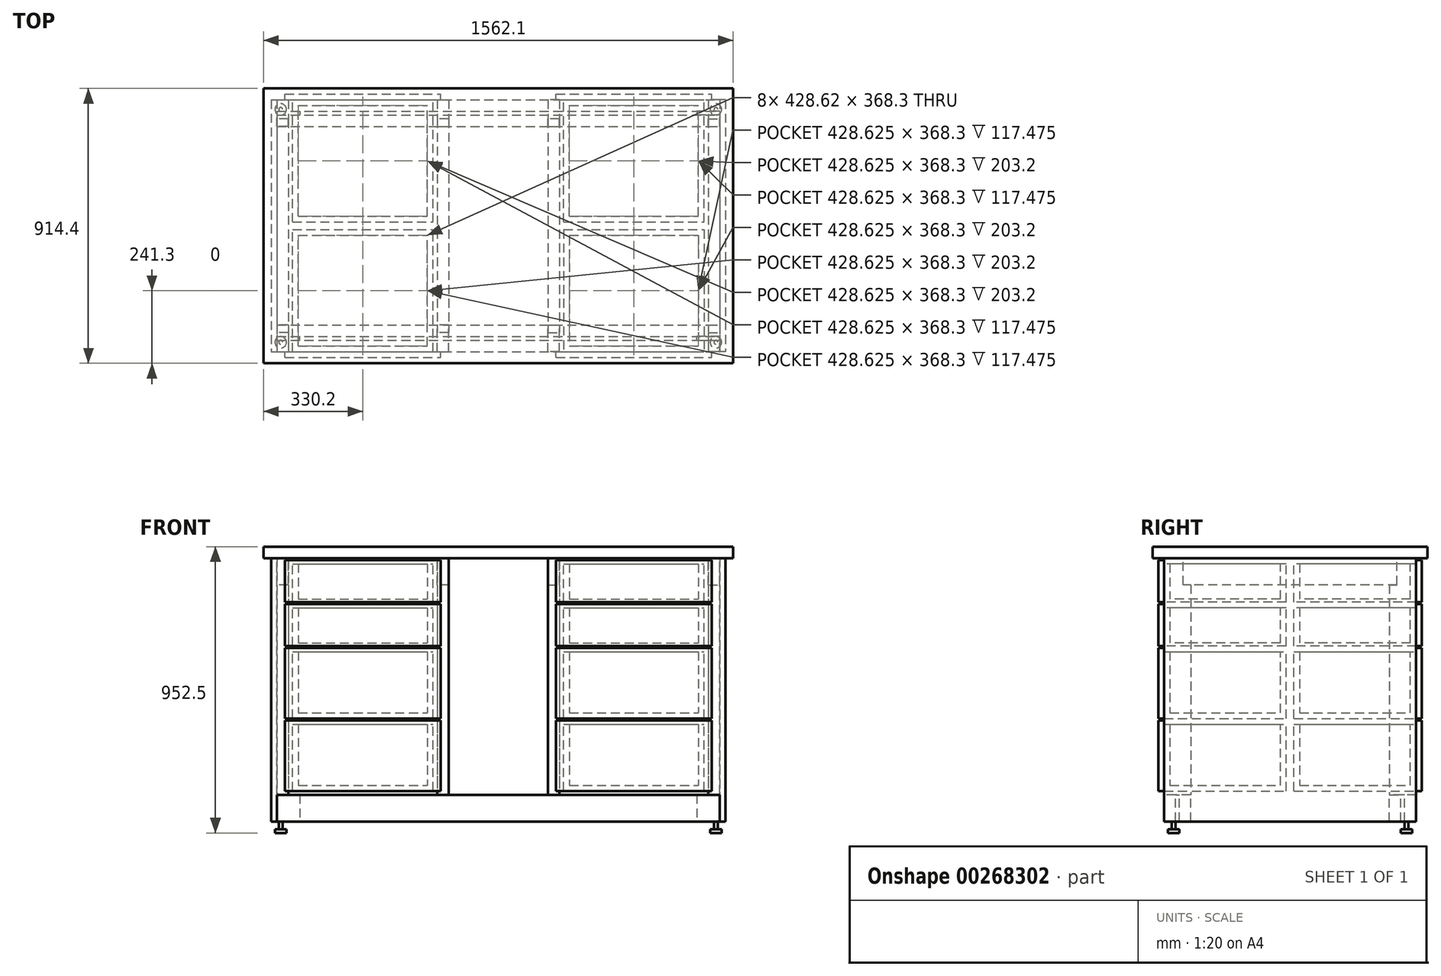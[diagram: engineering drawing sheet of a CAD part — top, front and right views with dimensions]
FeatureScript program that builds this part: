
annotation { "Feature Type Name" : "Feature", "Feature Type Description" : "" }
export const myFeature = defineFeature(function(context is Context, id is Id, definition is map)
    precondition{}
    {
        {
            var Q0;
            Q0=qCreatedBy(makeId("Top.planeOp"),FACE);
            var sketch = newSketch(context, id + "F0", { "sketchPlane" : qUnion([Q0])});
            skLineSegment(sketch, "E0.bottom", {"start": v(-736.6, 419.1) * mm, "end": v(-698.5, 419.1) * mm});
            skLineSegment(sketch, "E0.top", {"start": v(-736.6, 330.2) * mm, "end": v(-698.5, 330.2) * mm});
            skLineSegment(sketch, "E0.left", {"start": v(-736.6, 419.1) * mm, "end": v(-736.6, 330.2) * mm});
            skLineSegment(sketch, "E0.right", {"start": v(-698.5, 419.1) * mm, "end": v(-698.5, 330.2) * mm});
            skLineSegment(sketch, "E1.bottom", {"start": v(-736.6, -330.2) * mm, "end": v(-698.5, -330.2) * mm});
            skLineSegment(sketch, "E1.top", {"start": v(-736.6, -419.1) * mm, "end": v(-698.5, -419.1) * mm});
            skLineSegment(sketch, "E1.left", {"start": v(-736.6, -330.2) * mm, "end": v(-736.6, -419.1) * mm});
            skLineSegment(sketch, "E1.right", {"start": v(-698.5, -330.2) * mm, "end": v(-698.5, -419.1) * mm});
            skLineSegment(sketch, "E2.MirrorCS", {"start": v(698.5, 419.1) * mm, "end": v(698.5, 330.2) * mm});
            skLineSegment(sketch, "E3.MirrorCS", {"start": v(736.6, 330.2) * mm, "end": v(698.5, 330.2) * mm});
            skLineSegment(sketch, "E4.MirrorCS", {"start": v(736.6, 419.1) * mm, "end": v(736.6, 330.2) * mm});
            skLineSegment(sketch, "E5.MirrorCS", {"start": v(736.6, 419.1) * mm, "end": v(698.5, 419.1) * mm});
            skLineSegment(sketch, "E6.MirrorCS", {"start": v(736.6, -330.2) * mm, "end": v(698.5, -330.2) * mm});
            skLineSegment(sketch, "E7.MirrorCS", {"start": v(698.5, -330.2) * mm, "end": v(698.5, -419.1) * mm});
            skLineSegment(sketch, "E8.MirrorCS", {"start": v(736.6, -330.2) * mm, "end": v(736.6, -419.1) * mm});
            skLineSegment(sketch, "E9.MirrorCS", {"start": v(736.6, -419.1) * mm, "end": v(698.5, -419.1) * mm});
            skLineSegment(sketch, "E10.bottom", {"start": v(-203.2, 419.1) * mm, "end": v(-165.1, 419.1) * mm});
            skLineSegment(sketch, "E10.top", {"start": v(-203.2, 330.2) * mm, "end": v(-165.1, 330.2) * mm});
            skLineSegment(sketch, "E10.left", {"start": v(-203.2, 419.1) * mm, "end": v(-203.2, 330.2) * mm});
            skLineSegment(sketch, "E10.right", {"start": v(-165.1, 419.1) * mm, "end": v(-165.1, 330.2) * mm});
            skLineSegment(sketch, "E11.MirrorCS", {"start": v(-165.1, -419.1) * mm, "end": v(-165.1, -330.2) * mm});
            skLineSegment(sketch, "E12.MirrorCS", {"start": v(-203.2, -330.2) * mm, "end": v(-165.1, -330.2) * mm});
            skLineSegment(sketch, "E13.MirrorCS", {"start": v(-203.2, -419.1) * mm, "end": v(-203.2, -330.2) * mm});
            skLineSegment(sketch, "E14.MirrorCS", {"start": v(-203.2, -419.1) * mm, "end": v(-165.1, -419.1) * mm});
            skLineSegment(sketch, "E15", {"start": v(-736.6, 419.1) * mm, "end": v(736.6, 419.1) * mm, "construction": true});
            skLineSegment(sketch, "E16.MirrorCS", {"start": v(203.2, 330.2) * mm, "end": v(165.1, 330.2) * mm});
            skLineSegment(sketch, "E17.MirrorCS", {"start": v(203.2, 419.1) * mm, "end": v(165.1, 419.1) * mm});
            skLineSegment(sketch, "E18.MirrorCS", {"start": v(165.1, 419.1) * mm, "end": v(165.1, 330.2) * mm});
            skLineSegment(sketch, "E19.MirrorCS", {"start": v(203.2, 419.1) * mm, "end": v(203.2, 330.2) * mm});
            skLineSegment(sketch, "E20.MirrorCS", {"start": v(203.2, -419.1) * mm, "end": v(165.1, -419.1) * mm});
            skLineSegment(sketch, "E21.MirrorCS", {"start": v(165.1, -419.1) * mm, "end": v(165.1, -330.2) * mm});
            skLineSegment(sketch, "E22.MirrorCS", {"start": v(203.2, -330.2) * mm, "end": v(165.1, -330.2) * mm});
            skLineSegment(sketch, "E23.MirrorCS", {"start": v(203.2, -419.1) * mm, "end": v(203.2, -330.2) * mm});
            skSolve(sketch);
        }
        {
            var Q0;
            Q0=makeQuery(id+"F0.imprint","IMPRINT",FACE,{"disambiguationData":[TD([[makeQuery(id+"F0.imprint","IMPRINT",EDGE,{"derivedFrom":sQuery(id+"F0.wireOp",EDGE,"E0.bottom")}),-1.0]])]});
            var Q1;
            Q1=makeQuery(id+"F0.imprint","IMPRINT",FACE,{"disambiguationData":[TD([[makeQuery(id+"F0.imprint","IMPRINT",EDGE,{"derivedFrom":sQuery(id+"F0.wireOp",EDGE,"E2.MirrorCS")}),1.0]])]});
            var Q2;
            Q2=makeQuery(id+"F0.imprint","IMPRINT",FACE,{"disambiguationData":[TD([[makeQuery(id+"F0.imprint","IMPRINT",EDGE,{"derivedFrom":sQuery(id+"F0.wireOp",EDGE,"E6.MirrorCS")}),1.0]])]});
            var Q3;
            Q3=makeQuery(id+"F0.imprint","IMPRINT",FACE,{"disambiguationData":[TD([[makeQuery(id+"F0.imprint","IMPRINT",EDGE,{"derivedFrom":sQuery(id+"F0.wireOp",EDGE,"E1.bottom")}),-1.0]])]});
            var Q4;
            Q4=makeQuery(id+"F0.imprint","IMPRINT",FACE,{"disambiguationData":[TD([[makeQuery(id+"F0.imprint","IMPRINT",EDGE,{"derivedFrom":sQuery(id+"F0.wireOp",EDGE,"E10.bottom")}),-1.0]])]});
            var Q5;
            Q5=makeQuery(id+"F0.imprint","IMPRINT",FACE,{"disambiguationData":[TD([[makeQuery(id+"F0.imprint","IMPRINT",EDGE,{"derivedFrom":sQuery(id+"F0.wireOp",EDGE,"E16.MirrorCS")}),-1.0]])]});
            var Q6;
            Q6=makeQuery(id+"F0.imprint","IMPRINT",FACE,{"disambiguationData":[TD([[makeQuery(id+"F0.imprint","IMPRINT",EDGE,{"derivedFrom":sQuery(id+"F0.wireOp",EDGE,"E20.MirrorCS")}),-1.0]])]});
            var Q7;
            Q7=makeQuery(id+"F0.imprint","IMPRINT",FACE,{"disambiguationData":[TD([[makeQuery(id+"F0.imprint","IMPRINT",EDGE,{"derivedFrom":sQuery(id+"F0.wireOp",EDGE,"E11.MirrorCS")}),1.0]])]});
            extrude(context, id + "F1", {"entities" : qUnion([Q0, Q1, Q2, Q3, Q4, Q5, Q6, Q7]), "depth" : 787.4 * mm});
        }
        {
            var Q0;
            Q0=makeQuery(id+"F1.opExtrude","CAP_FACE",FACE,{"disambiguationData":[OSD([sQuery(id+"F0.wireOp",EDGE,"E1.bottom"),sQuery(id+"F0.wireOp",EDGE,"E1.top"),sQuery(id+"F0.wireOp",EDGE,"E1.left"),sQuery(id+"F0.wireOp",EDGE,"E1.right")])],"isStart":true});
            var sketch = newSketch(context, id + "F2", { "sketchPlane" : qUnion([Q0])});
            skLineSegment(sketch, "E24.bottom", {"start": v(-736.6, 419.1) * mm, "end": v(736.6, 419.1) * mm});
            skLineSegment(sketch, "E24.top", {"start": v(-736.6, 381) * mm, "end": v(736.6, 381) * mm});
            skLineSegment(sketch, "E24.left", {"start": v(-736.6, 419.1) * mm, "end": v(-736.6, 381) * mm});
            skLineSegment(sketch, "E24.right", {"start": v(736.6, 419.1) * mm, "end": v(736.6, 381) * mm});
            skLineSegment(sketch, "E25.bottom", {"start": v(-736.6, 330.2) * mm, "end": v(736.6, 330.2) * mm});
            skLineSegment(sketch, "E25.top", {"start": v(-736.6, 368.3) * mm, "end": v(736.6, 368.3) * mm});
            skLineSegment(sketch, "E25.left", {"start": v(-736.6, 330.2) * mm, "end": v(-736.6, 368.3) * mm});
            skLineSegment(sketch, "E25.right", {"start": v(736.6, 330.2) * mm, "end": v(736.6, 368.3) * mm});
            skLineSegment(sketch, "E26.MirrorCS", {"start": v(-736.6, -330.2) * mm, "end": v(736.6, -330.2) * mm});
            skLineSegment(sketch, "E27.MirrorCS", {"start": v(-736.6, -368.3) * mm, "end": v(736.6, -368.3) * mm});
            skLineSegment(sketch, "E28.MirrorCS", {"start": v(-736.6, -330.2) * mm, "end": v(-736.6, -368.3) * mm});
            skLineSegment(sketch, "E29.MirrorCS", {"start": v(736.6, -330.2) * mm, "end": v(736.6, -368.3) * mm});
            skLineSegment(sketch, "E30.MirrorCS", {"start": v(736.6, -419.1) * mm, "end": v(736.6, -381) * mm});
            skLineSegment(sketch, "E31.MirrorCS", {"start": v(-736.6, -419.1) * mm, "end": v(736.6, -419.1) * mm});
            skLineSegment(sketch, "E32.MirrorCS", {"start": v(-736.6, -381) * mm, "end": v(736.6, -381) * mm});
            skLineSegment(sketch, "E33.MirrorCS", {"start": v(-736.6, -419.1) * mm, "end": v(-736.6, -381) * mm});
            skSolve(sketch);
        }
        {
            var Q0;
            {var subQ0=sQuery(id+"F2.wireOp",EDGE,"E25.left");Q0=makeQuery(id+"F2.imprint","IMPRINT",FACE,{"disambiguationData":[TD([[makeQuery(id+"F2.imprint","IMPRINT",EDGE,{"derivedFrom":subQ0}),-1.0]])]});}
            var Q1;
            {var subQ3=sQuery(id+"F2.wireOp",EDGE,"E25.right");Q1=makeQuery(id+"F2.imprint","IMPRINT",FACE,{"disambiguationData":[TD([[makeQuery(id+"F2.imprint","IMPRINT",EDGE,{"derivedFrom":subQ3}),1.0]])]});}
            var Q2;
            {var subQ3=sQuery(id+"F2.wireOp",EDGE,"E24.right");Q2=makeQuery(id+"F2.imprint","IMPRINT",FACE,{"disambiguationData":[TD([[makeQuery(id+"F2.imprint","IMPRINT",EDGE,{"derivedFrom":subQ3}),-1.0]])]});}
            var Q3;
            {var subQ0=sQuery(id+"F2.wireOp",EDGE,"E24.left");Q3=makeQuery(id+"F2.imprint","IMPRINT",FACE,{"disambiguationData":[TD([[makeQuery(id+"F2.imprint","IMPRINT",EDGE,{"derivedFrom":subQ0}),-1.0]])]});}
            var Q4;
            Q4=makeQuery(id+"F2.imprint","IMPRINT",FACE,{"disambiguationData":[TD([[makeQuery(id+"F2.imprint","IMPRINT",EDGE,{"derivedFrom":sQuery(id+"F2.wireOp",EDGE,"E26.MirrorCS")}),-1.0]])]});
            var Q5;
            Q5=makeQuery(id+"F2.imprint","IMPRINT",FACE,{"disambiguationData":[TD([[makeQuery(id+"F2.imprint","IMPRINT",EDGE,{"derivedFrom":sQuery(id+"F2.wireOp",EDGE,"E30.MirrorCS")}),1.0]])]});
            extrude(context, id + "F3", {"entities" : qUnion([Q0, Q1, Q2, Q3, Q4, Q5]), "depth" : 88.9 * mm});
        }
        {
            var Q0;
            Q0=makeQuery(id+"F1.opExtrude","CAP_FACE",FACE,{"disambiguationData":[OSD([sQuery(id+"F0.wireOp",EDGE,"E0.bottom"),sQuery(id+"F0.wireOp",EDGE,"E0.top"),sQuery(id+"F0.wireOp",EDGE,"E0.left"),sQuery(id+"F0.wireOp",EDGE,"E0.right")])],"isStart":false});
            var sketch = newSketch(context, id + "F4", { "sketchPlane" : qUnion([Q0])});
            skLineSegment(sketch, "E34.bottom", {"start": v(-755.65, 419.1) * mm, "end": v(-736.6, 419.1) * mm});
            skLineSegment(sketch, "E34.top", {"start": v(-755.65, -419.1) * mm, "end": v(-736.6, -419.1) * mm});
            skLineSegment(sketch, "E34.left", {"start": v(-755.65, 419.1) * mm, "end": v(-755.65, -419.1) * mm});
            skLineSegment(sketch, "E34.right", {"start": v(-736.6, 419.1) * mm, "end": v(-736.6, -419.1) * mm});
            skLineSegment(sketch, "E35.MirrorCS", {"start": v(755.65, 419.1) * mm, "end": v(736.6, 419.1) * mm});
            skLineSegment(sketch, "E36.MirrorCS", {"start": v(755.65, -419.1) * mm, "end": v(736.6, -419.1) * mm});
            skLineSegment(sketch, "E37.MirrorCS", {"start": v(736.6, 419.1) * mm, "end": v(736.6, -419.1) * mm});
            skLineSegment(sketch, "E38.MirrorCS", {"start": v(755.65, 419.1) * mm, "end": v(755.65, -419.1) * mm});
            skSolve(sketch);
        }
        {
            var Q0;
            Q0=makeQuery(id+"F4.imprint","IMPRINT",FACE,{"disambiguationData":[TD([[makeQuery(id+"F4.imprint","IMPRINT",EDGE,{"derivedFrom":sQuery(id+"F4.wireOp",EDGE,"E35.MirrorCS")}),1.0]])]});
            var Q1;
            {var subQ3=sQuery(id+"F4.wireOp",EDGE,"E34.bottom");Q1=makeQuery(id+"F4.imprint","IMPRINT",FACE,{"disambiguationData":[TD([[makeQuery(id+"F4.imprint","IMPRINT",EDGE,{"derivedFrom":subQ3}),-1.0]])]});}
            var Q2;
            Q2=makeQuery(id+"F3.opExtrude","CAP_FACE",FACE,{"disambiguationData":[OSD([sQuery(id+"F2.wireOp",EDGE,"E30.MirrorCS"),sQuery(id+"F2.wireOp",EDGE,"E31.MirrorCS"),sQuery(id+"F2.wireOp",EDGE,"E32.MirrorCS"),sQuery(id+"F2.wireOp",EDGE,"E33.MirrorCS")])],"isStart":false});
            extrude(context, id + "F5", {"entities" : qUnion([Q0, Q1]), "oppositeDirection" : true, "endBoundEntityFace" : qUnion([Q2]), "depth" : 876.3 * mm});
        }
        {
            var Q0;
            Q0=makeQuery(id+"F1.opExtrude","CAP_FACE",FACE,{"disambiguationData":[OSD([sQuery(id+"F0.wireOp",EDGE,"E10.bottom"),sQuery(id+"F0.wireOp",EDGE,"E10.top"),sQuery(id+"F0.wireOp",EDGE,"E10.left"),sQuery(id+"F0.wireOp",EDGE,"E10.right")])],"isStart":false});
            var sketch = newSketch(context, id + "F6", { "sketchPlane" : qUnion([Q0])});
            skLineSegment(sketch, "E39.bottom", {"start": v(-698.5, 330.2) * mm, "end": v(-736.6, 330.2) * mm});
            skLineSegment(sketch, "E39.top", {"start": v(-698.5, 355.6) * mm, "end": v(-736.6, 355.6) * mm});
            skLineSegment(sketch, "E39.left", {"start": v(-698.5, 330.2) * mm, "end": v(-698.5, 355.6) * mm});
            skLineSegment(sketch, "E39.right", {"start": v(-736.6, 330.2) * mm, "end": v(-736.6, 355.6) * mm});
            skLineSegment(sketch, "E40.bottom", {"start": v(-165.1, 330.2) * mm, "end": v(-203.2, 330.2) * mm});
            skLineSegment(sketch, "E40.top", {"start": v(-165.1, 355.6) * mm, "end": v(-203.2, 355.6) * mm});
            skLineSegment(sketch, "E40.left", {"start": v(-165.1, 330.2) * mm, "end": v(-165.1, 355.6) * mm});
            skLineSegment(sketch, "E40.right", {"start": v(-203.2, 330.2) * mm, "end": v(-203.2, 355.6) * mm});
            skLineSegment(sketch, "E41.MirrorCS", {"start": v(203.2, 330.2) * mm, "end": v(203.2, 355.6) * mm});
            skLineSegment(sketch, "E42.MirrorCS", {"start": v(165.1, 330.2) * mm, "end": v(165.1, 355.6) * mm});
            skLineSegment(sketch, "E43.MirrorCS", {"start": v(698.5, 330.2) * mm, "end": v(698.5, 355.6) * mm});
            skLineSegment(sketch, "E44.MirrorCS", {"start": v(736.6, 330.2) * mm, "end": v(736.6, 355.6) * mm});
            skLineSegment(sketch, "E45.MirrorCS", {"start": v(698.5, 355.6) * mm, "end": v(736.6, 355.6) * mm});
            skLineSegment(sketch, "E46.MirrorCS", {"start": v(165.1, 330.2) * mm, "end": v(203.2, 330.2) * mm});
            skLineSegment(sketch, "E47.MirrorCS", {"start": v(698.5, 330.2) * mm, "end": v(736.6, 330.2) * mm});
            skLineSegment(sketch, "E48.MirrorCS", {"start": v(165.1, 355.6) * mm, "end": v(203.2, 355.6) * mm});
            skLineSegment(sketch, "E49.MirrorCS", {"start": v(736.6, -330.2) * mm, "end": v(736.6, -355.6) * mm});
            skLineSegment(sketch, "E50.MirrorCS", {"start": v(698.5, -330.2) * mm, "end": v(698.5, -355.6) * mm});
            skLineSegment(sketch, "E51.MirrorCS", {"start": v(165.1, -330.2) * mm, "end": v(165.1, -355.6) * mm});
            skLineSegment(sketch, "E52.MirrorCS", {"start": v(203.2, -330.2) * mm, "end": v(203.2, -355.6) * mm});
            skLineSegment(sketch, "E53.MirrorCS", {"start": v(-203.2, -330.2) * mm, "end": v(-203.2, -355.6) * mm});
            skLineSegment(sketch, "E54.MirrorCS", {"start": v(-165.1, -330.2) * mm, "end": v(-165.1, -355.6) * mm});
            skLineSegment(sketch, "E55.MirrorCS", {"start": v(-698.5, -330.2) * mm, "end": v(-698.5, -355.6) * mm});
            skLineSegment(sketch, "E56.MirrorCS", {"start": v(-736.6, -330.2) * mm, "end": v(-736.6, -355.6) * mm});
            skLineSegment(sketch, "E57.MirrorCS", {"start": v(698.5, -355.6) * mm, "end": v(736.6, -355.6) * mm});
            skLineSegment(sketch, "E58.MirrorCS", {"start": v(-165.1, -355.6) * mm, "end": v(-203.2, -355.6) * mm});
            skLineSegment(sketch, "E59.MirrorCS", {"start": v(165.1, -330.2) * mm, "end": v(203.2, -330.2) * mm});
            skLineSegment(sketch, "E60.MirrorCS", {"start": v(-698.5, -355.6) * mm, "end": v(-736.6, -355.6) * mm});
            skLineSegment(sketch, "E61.MirrorCS", {"start": v(-698.5, -330.2) * mm, "end": v(-736.6, -330.2) * mm});
            skLineSegment(sketch, "E62.MirrorCS", {"start": v(698.5, -330.2) * mm, "end": v(736.6, -330.2) * mm});
            skLineSegment(sketch, "E63.MirrorCS", {"start": v(-165.1, -330.2) * mm, "end": v(-203.2, -330.2) * mm});
            skLineSegment(sketch, "E64.MirrorCS", {"start": v(165.1, -355.6) * mm, "end": v(203.2, -355.6) * mm});
            skSolve(sketch);
        }
        {
            var Q0;
            Q0=makeQuery(id+"F6.imprint","IMPRINT",FACE,{"disambiguationData":[TD([[makeQuery(id+"F6.imprint","IMPRINT",EDGE,{"derivedFrom":sQuery(id+"F6.wireOp",EDGE,"E39.bottom")}),-1.0]])]});
            var Q1;
            Q1=makeQuery(id+"F6.imprint","IMPRINT",FACE,{"disambiguationData":[TD([[makeQuery(id+"F6.imprint","IMPRINT",EDGE,{"derivedFrom":sQuery(id+"F6.wireOp",EDGE,"E40.bottom")}),1.0]])]});
            var Q2;
            Q2=makeQuery(id+"F6.imprint","IMPRINT",FACE,{"disambiguationData":[TD([[makeQuery(id+"F6.imprint","IMPRINT",EDGE,{"derivedFrom":sQuery(id+"F6.wireOp",EDGE,"E41.MirrorCS")}),1.0]])]});
            var Q3;
            Q3=makeQuery(id+"F6.imprint","IMPRINT",FACE,{"disambiguationData":[TD([[makeQuery(id+"F6.imprint","IMPRINT",EDGE,{"derivedFrom":sQuery(id+"F6.wireOp",EDGE,"E43.MirrorCS")}),-1.0]])]});
            var Q4;
            Q4=makeQuery(id+"F6.imprint","IMPRINT",FACE,{"disambiguationData":[TD([[makeQuery(id+"F6.imprint","IMPRINT",EDGE,{"derivedFrom":sQuery(id+"F6.wireOp",EDGE,"E49.MirrorCS")}),-1.0]])]});
            var Q5;
            Q5=makeQuery(id+"F6.imprint","IMPRINT",FACE,{"disambiguationData":[TD([[makeQuery(id+"F6.imprint","IMPRINT",EDGE,{"derivedFrom":sQuery(id+"F6.wireOp",EDGE,"E51.MirrorCS")}),1.0]])]});
            var Q6;
            Q6=makeQuery(id+"F6.imprint","IMPRINT",FACE,{"disambiguationData":[TD([[makeQuery(id+"F6.imprint","IMPRINT",EDGE,{"derivedFrom":sQuery(id+"F6.wireOp",EDGE,"E53.MirrorCS")}),1.0]])]});
            var Q7;
            Q7=makeQuery(id+"F6.imprint","IMPRINT",FACE,{"disambiguationData":[TD([[makeQuery(id+"F6.imprint","IMPRINT",EDGE,{"derivedFrom":sQuery(id+"F6.wireOp",EDGE,"E55.MirrorCS")}),-1.0]])]});
            extrude(context, id + "F7", {"entities" : qUnion([Q0, Q1, Q2, Q3, Q4, Q5, Q6, Q7]), "operationType" : NewBodyOperationType.REMOVE, "oppositeDirection" : true, "depth" : 88.9 * mm});
        }
        {
            var Q0;
            Q0=makeQuery(id+"F7.boolean.opBoolean","COPY",FACE,{"derivedFrom":makeQuery(id+"F7.opExtrude","CAP_FACE",FACE,{"disambiguationData":[OSD([sQuery(id+"F6.wireOp",EDGE,"E39.bottom"),sQuery(id+"F6.wireOp",EDGE,"E39.top"),sQuery(id+"F6.wireOp",EDGE,"E39.left"),sQuery(id+"F6.wireOp",EDGE,"E39.right")])],"isStart":false})});
            var sketch = newSketch(context, id + "F8", { "sketchPlane" : qUnion([Q0])});
            skLineSegment(sketch, "E65.bottom", {"start": v(-736.6, 355.6) * mm, "end": v(-698.5, 355.6) * mm});
            skLineSegment(sketch, "E65.top", {"start": v(-736.6, -355.6) * mm, "end": v(-698.5, -355.6) * mm});
            skLineSegment(sketch, "E65.left", {"start": v(-736.6, 355.6) * mm, "end": v(-736.6, -355.6) * mm});
            skLineSegment(sketch, "E65.right", {"start": v(-698.5, 355.6) * mm, "end": v(-698.5, -355.6) * mm});
            skLineSegment(sketch, "E66.bottom", {"start": v(-203.2, 355.6) * mm, "end": v(-165.1, 355.6) * mm});
            skLineSegment(sketch, "E66.top", {"start": v(-203.2, -355.6) * mm, "end": v(-165.1, -355.6) * mm});
            skLineSegment(sketch, "E66.left", {"start": v(-203.2, 355.6) * mm, "end": v(-203.2, -355.6) * mm});
            skLineSegment(sketch, "E66.right", {"start": v(-165.1, 355.6) * mm, "end": v(-165.1, -355.6) * mm});
            skLineSegment(sketch, "E67.MirrorCS", {"start": v(203.2, 355.6) * mm, "end": v(165.1, 355.6) * mm});
            skLineSegment(sketch, "E68.MirrorCS", {"start": v(203.2, -355.6) * mm, "end": v(165.1, -355.6) * mm});
            skLineSegment(sketch, "E69.MirrorCS", {"start": v(736.6, 355.6) * mm, "end": v(698.5, 355.6) * mm});
            skLineSegment(sketch, "E70.MirrorCS", {"start": v(736.6, -355.6) * mm, "end": v(698.5, -355.6) * mm});
            skLineSegment(sketch, "E71.MirrorCS", {"start": v(736.6, 355.6) * mm, "end": v(736.6, -355.6) * mm});
            skLineSegment(sketch, "E72.MirrorCS", {"start": v(698.5, 355.6) * mm, "end": v(698.5, -355.6) * mm});
            skLineSegment(sketch, "E73.MirrorCS", {"start": v(203.2, 355.6) * mm, "end": v(203.2, -355.6) * mm});
            skLineSegment(sketch, "E74.MirrorCS", {"start": v(165.1, 355.6) * mm, "end": v(165.1, -355.6) * mm});
            skSolve(sketch);
        }
        {
            var Q0;
            {var subQ0=sQuery(id+"F8.wireOp",EDGE,"E65.top");Q0=makeQuery(id+"F8.imprint","IMPRINT",FACE,{"disambiguationData":[TD([[makeQuery(id+"F8.imprint","IMPRINT",EDGE,{"derivedFrom":subQ0}),1.0]])]});}
            var Q1;
            Q1=makeQuery(id+"F8.imprint","IMPRINT",FACE,{"disambiguationData":[TD([[makeQuery(id+"F8.imprint","IMPRINT",EDGE,{"derivedFrom":sQuery(id+"F8.wireOp",EDGE,"E66.bottom")}),-1.0]])]});
            var Q2;
            Q2=makeQuery(id+"F8.imprint","IMPRINT",FACE,{"disambiguationData":[TD([[makeQuery(id+"F8.imprint","IMPRINT",EDGE,{"derivedFrom":sQuery(id+"F8.wireOp",EDGE,"E67.MirrorCS")}),1.0]])]});
            var Q3;
            Q3=makeQuery(id+"F8.imprint","IMPRINT",FACE,{"disambiguationData":[TD([[makeQuery(id+"F8.imprint","IMPRINT",EDGE,{"derivedFrom":sQuery(id+"F8.wireOp",EDGE,"E69.MirrorCS")}),1.0]])]});
            var Q4;
            {var subQ0=sQuery(id+"F8.wireOp",EDGE,"E65.bottom");Q4=makeQuery(id+"F8.imprint","IMPRINT",FACE,{"disambiguationData":[TD([[makeQuery(id+"F8.imprint","IMPRINT",EDGE,{"derivedFrom":subQ0}),1.0]])]});}
            extrude(context, id + "F9", {"entities" : qUnion([Q0, Q1, Q2, Q3, Q4]), "depth" : 88.9 * mm});
        }
        {
            var Q0;
            Q0=makeQuery(id+"F1.opExtrude","SWEPT_FACE",FACE,{"disambiguationData":[OSD([sQuery(id+"F0.wireOp",EDGE,"E1.top")])]});
            var sketch = newSketch(context, id + "F10", { "sketchPlane" : qUnion([Q0])});
            skLineSegment(sketch, "E75.bottom", {"start": v(-781.05, 806.45) * mm, "end": v(781.05, 806.45) * mm});
            skLineSegment(sketch, "E75.top", {"start": v(-781.05, 787.4) * mm, "end": v(781.05, 787.4) * mm});
            skLineSegment(sketch, "E75.left", {"start": v(-781.05, 806.45) * mm, "end": v(-781.05, 787.4) * mm});
            skLineSegment(sketch, "E75.right", {"start": v(781.05, 806.45) * mm, "end": v(781.05, 787.4) * mm});
            skLineSegment(sketch, "E76.top", {"start": v(-781.05, 825.5) * mm, "end": v(781.05, 825.5) * mm});
            skLineSegment(sketch, "E76.left", {"start": v(-781.05, 806.45) * mm, "end": v(-781.05, 825.5) * mm});
            skLineSegment(sketch, "E76.right", {"start": v(781.05, 806.45) * mm, "end": v(781.05, 825.5) * mm});
            skSolve(sketch);
        }
        {
            var Q0;
            {var subQ0=sQuery(id+"F10.wireOp",EDGE,"E75.left");Q0=makeQuery(id+"F10.imprint","IMPRINT",FACE,{"disambiguationData":[TD([[makeQuery(id+"F10.imprint","IMPRINT",EDGE,{"derivedFrom":subQ0}),1.0]])]});}
            extrude(context, id + "F11", {"entities" : qUnion([Q0]), "oppositeDirection" : true, "depth" : 876.3 * mm});
        }
        {
            var Q0;
            {var subQ0=sQuery(id+"F10.wireOp",EDGE,"E75.left");Q0=makeQuery(id+"F10.imprint","IMPRINT",FACE,{"disambiguationData":[TD([[makeQuery(id+"F10.imprint","IMPRINT",EDGE,{"derivedFrom":subQ0}),1.0]])]});}
            extrude(context, id + "F12", {"entities" : qUnion([Q0]), "operationType" : NewBodyOperationType.ADD, "depth" : 38.1 * mm});
        }
        {
            var Q0;
            Q0=makeQuery(id+"F10.imprint","IMPRINT",FACE,{"disambiguationData":[TD([[makeQuery(id+"F10.imprint","IMPRINT",EDGE,{"derivedFrom":sQuery(id+"F10.wireOp",EDGE,"E75.bottom")}),1.0]])]});
            extrude(context, id + "F13", {"entities" : qUnion([Q0]), "oppositeDirection" : true, "depth" : 876.3 * mm});
        }
        {
            var Q0;
            Q0=makeQuery(id+"F10.imprint","IMPRINT",FACE,{"disambiguationData":[TD([[makeQuery(id+"F10.imprint","IMPRINT",EDGE,{"derivedFrom":sQuery(id+"F10.wireOp",EDGE,"E75.bottom")}),1.0]])]});
            extrude(context, id + "F14", {"entities" : qUnion([Q0]), "operationType" : NewBodyOperationType.ADD, "depth" : 38.1 * mm});
        }
        {
            var Q0;
            Q0=makeQuery(id+"F1.opExtrude","SWEPT_FACE",FACE,{"disambiguationData":[OSD([sQuery(id+"F0.wireOp",EDGE,"E1.top")])]});
            var sketch = newSketch(context, id + "F15", { "sketchPlane" : qUnion([Q0])});
            skLineSegment(sketch, "E77.bottom", {"start": v(-665.16, 768.35) * mm, "end": v(-236.54, 768.35) * mm});
            skLineSegment(sketch, "E77.top", {"start": v(-665.16, 641.35) * mm, "end": v(-236.54, 641.35) * mm});
            skLineSegment(sketch, "E77.left", {"start": v(-665.16, 768.35) * mm, "end": v(-665.16, 641.35) * mm});
            skLineSegment(sketch, "E77.right", {"start": v(-236.54, 768.35) * mm, "end": v(-236.54, 641.35) * mm});
            skLineSegment(sketch, "E78", {"start": v(236.55, 845.3) * mm, "end": v(236.55, 324.47) * mm, "construction": true});
            skSolve(sketch);
        }
        {
            var Q0;
            Q0=makeQuery(id+"F15.imprint","IMPRINT",FACE,{"disambiguationData":[TD([[makeQuery(id+"F15.imprint","IMPRINT",EDGE,{"derivedFrom":sQuery(id+"F15.wireOp",EDGE,"E77.bottom")}),-1.0]])]});
            extrude(context, id + "F16", {"entities" : qUnion([Q0]), "oppositeDirection" : true, "depth" : 19.05 * mm});
        }
        {
            var Q0;
            Q0=makeQuery(id+"F16.opExtrude","SWEPT_FACE",FACE,{"disambiguationData":[OSD([sQuery(id+"F15.wireOp",EDGE,"E77.bottom")])]});
            var sketch = newSketch(context, id + "F17", { "sketchPlane" : qUnion([Q0])});
            skLineSegment(sketch, "E79.bottom", {"start": v(-236.54, -31.75) * mm, "end": v(-217.49, -31.75) * mm});
            skLineSegment(sketch, "E79.top", {"start": v(-236.54, -419.1) * mm, "end": v(-217.49, -419.1) * mm});
            skLineSegment(sketch, "E79.left", {"start": v(-236.54, -31.75) * mm, "end": v(-236.54, -419.1) * mm});
            skLineSegment(sketch, "E79.right", {"start": v(-217.49, -31.75) * mm, "end": v(-217.49, -419.1) * mm});
            skLineSegment(sketch, "E80", {"start": v(-450.85, -400.05) * mm, "end": v(-450.85, -33.72) * mm, "construction": true});
            skLineSegment(sketch, "E81.MirrorCS", {"start": v(-665.16, -31.75) * mm, "end": v(-684.21, -31.75) * mm});
            skLineSegment(sketch, "E82.MirrorCS", {"start": v(-665.16, -419.1) * mm, "end": v(-684.21, -419.1) * mm});
            skLineSegment(sketch, "E83.MirrorCS", {"start": v(-684.21, -31.75) * mm, "end": v(-684.21, -419.1) * mm});
            skLineSegment(sketch, "E84.MirrorCS", {"start": v(-665.16, -31.75) * mm, "end": v(-665.16, -419.1) * mm});
            skLineSegment(sketch, "E85.bottom", {"start": v(-684.21, -31.75) * mm, "end": v(-217.49, -31.75) * mm});
            skLineSegment(sketch, "E85.top", {"start": v(-684.21, -12.7) * mm, "end": v(-217.49, -12.7) * mm});
            skLineSegment(sketch, "E85.left", {"start": v(-684.21, -31.75) * mm, "end": v(-684.21, -12.7) * mm});
            skLineSegment(sketch, "E85.right", {"start": v(-217.49, -31.75) * mm, "end": v(-217.49, -12.7) * mm});
            skSolve(sketch);
        }
        {
            var Q0;
            {var subQ3=sQuery(id+"F17.wireOp",EDGE,"E81.MirrorCS");Q0=makeQuery(id+"F17.imprint","IMPRINT",FACE,{"disambiguationData":[TD([[makeQuery(id+"F17.imprint","IMPRINT",EDGE,{"derivedFrom":subQ3}),1.0]])]});}
            var Q1;
            {var subQ4=sQuery(id+"F17.wireOp",EDGE,"E79.bottom");Q1=makeQuery(id+"F17.imprint","IMPRINT",FACE,{"disambiguationData":[TD([[makeQuery(id+"F17.imprint","IMPRINT",EDGE,{"derivedFrom":subQ4}),-1.0]])]});}
            var Q2;
            Q2=makeQuery(id+"F17.imprint","IMPRINT",FACE,{"disambiguationData":[TD([[makeQuery(id+"F17.imprint","IMPRINT",EDGE,{"derivedFrom":sQuery(id+"F17.wireOp",EDGE,"E85.top")}),-1.0]])]});
            var Q3;
            {var subQ1=sQuery(id+"F17.wireOp",EDGE,"E82.MirrorCS");Q3=makeQuery(id+"F17.imprint","IMPRINT",FACE,{"disambiguationData":[TD([[makeQuery(id+"F17.imprint","IMPRINT",EDGE,{"derivedFrom":subQ1}),-1.0]])]});}
            var Q4;
            {var subQ2=sQuery(id+"F17.wireOp",EDGE,"E79.top");Q4=makeQuery(id+"F17.imprint","IMPRINT",FACE,{"disambiguationData":[TD([[makeQuery(id+"F17.imprint","IMPRINT",EDGE,{"derivedFrom":subQ2}),1.0]])]});}
            extrude(context, id + "F18", {"entities" : qUnion([Q0, Q1, Q2, Q3, Q4]), "operationType" : NewBodyOperationType.ADD, "oppositeDirection" : true, "depth" : 127 * mm});
        }
        {
            var Q0;
            Q0=makeQuery(id+"F18.boolean.opBoolean","MERGE",FACE,{"derivedFrom":[makeQuery(id+"F16.opExtrude","SWEPT_FACE",FACE,{"disambiguationData":[OSD([sQuery(id+"F15.wireOp",EDGE,"E77.top")])]}),makeQuery(id+"F18.opExtrude","CAP_FACE",FACE,{"disambiguationData":[OSD([sQuery(id+"F17.wireOp",EDGE,"E79.top"),sQuery(id+"F17.wireOp",EDGE,"E79.left"),sQuery(id+"F17.wireOp",EDGE,"E79.right"),sQuery(id+"F17.wireOp",EDGE,"E82.MirrorCS"),sQuery(id+"F17.wireOp",EDGE,"E83.MirrorCS"),sQuery(id+"F17.wireOp",EDGE,"E84.MirrorCS"),sQuery(id+"F17.wireOp",EDGE,"E85.bottom"),sQuery(id+"F17.wireOp",EDGE,"E85.top"),sQuery(id+"F17.wireOp",EDGE,"E85.left"),sQuery(id+"F17.wireOp",EDGE,"E85.right")])],"isStart":false})]});
            var sketch = newSketch(context, id + "F19", { "sketchPlane" : qUnion([Q0])});
            skLineSegment(sketch, "E86.bottom", {"start": v(-665.16, 400.05) * mm, "end": v(-236.54, 400.05) * mm});
            skLineSegment(sketch, "E86.top", {"start": v(-665.16, 31.75) * mm, "end": v(-236.54, 31.75) * mm});
            skLineSegment(sketch, "E86.left", {"start": v(-665.16, 400.05) * mm, "end": v(-665.16, 31.75) * mm});
            skLineSegment(sketch, "E86.right", {"start": v(-236.54, 400.05) * mm, "end": v(-236.54, 31.75) * mm});
            skSolve(sketch);
        }
        {
            var Q0;
            Q0=makeQuery(id+"F19.imprint","IMPRINT",FACE,{"disambiguationData":[TD([[makeQuery(id+"F19.imprint","IMPRINT",EDGE,{"derivedFrom":sQuery(id+"F19.wireOp",EDGE,"E86.bottom")}),-1.0]])]});
            extrude(context, id + "F20", {"entities" : qUnion([Q0]), "operationType" : NewBodyOperationType.ADD, "oppositeDirection" : true, "depth" : 9.52 * mm});
        }
        {
            var Q0;
            Q0=makeQuery(id+"F18.boolean.opBoolean","MERGE",FACE,{"derivedFrom":[makeQuery(id+"F16.opExtrude","CAP_FACE",FACE,{"disambiguationData":[OSD([sQuery(id+"F15.wireOp",EDGE,"E77.bottom"),sQuery(id+"F15.wireOp",EDGE,"E77.top"),sQuery(id+"F15.wireOp",EDGE,"E77.left"),sQuery(id+"F15.wireOp",EDGE,"E77.right")])],"isStart":true}),makeQuery(id+"F18.opExtrude","SWEPT_FACE",FACE,{"disambiguationData":[OSD([sQuery(id+"F17.wireOp",EDGE,"E79.top")])]}),makeQuery(id+"F18.opExtrude","SWEPT_FACE",FACE,{"disambiguationData":[OSD([sQuery(id+"F17.wireOp",EDGE,"E82.MirrorCS")])]})]});
            var sketch = newSketch(context, id + "F21", { "sketchPlane" : qUnion([Q0])});
            skLineSegment(sketch, "E87.bottom", {"start": v(-709.61, 781.05) * mm, "end": v(-192.09, 781.05) * mm});
            skLineSegment(sketch, "E87.top", {"start": v(-709.61, 641.35) * mm, "end": v(-192.09, 641.35) * mm});
            skLineSegment(sketch, "E87.left", {"start": v(-709.61, 781.05) * mm, "end": v(-709.61, 641.35) * mm});
            skLineSegment(sketch, "E87.right", {"start": v(-192.09, 781.05) * mm, "end": v(-192.09, 641.35) * mm});
            skSolve(sketch);
        }
        {
            var Q0;
            {var subQ1=sQuery(id+"F17.wireOp",EDGE,"E79.top");var subQ2=makeQuery(id+"F18.opExtrude","SWEPT_EDGE",EDGE,{"disambiguationData":[OSD([subQ1,sQuery(id+"F17.wireOp",EDGE,"E79.right")])]});Q0=makeQuery(id+"F21.imprint","IMPRINT",FACE,{"disambiguationData":[TD([[makeQuery(id+"F21.imprint","IMPRINT",EDGE,{"derivedFrom":subQ2}),1.0]])]});}
            var Q1;
            Q1=makeQuery(id+"F21.imprint","IMPRINT",FACE,{"disambiguationData":[TD([[makeQuery(id+"F21.imprint","IMPRINT",EDGE,{"derivedFrom":sQuery(id+"F21.wireOp",EDGE,"E87.bottom")}),-1.0]])]});
            extrude(context, id + "F22", {"entities" : qUnion([Q0, Q1]), "depth" : 19.05 * mm});
        }
        {
            var Q0;
            Q0=makeQuery(id+"F16.opExtrude","SWEPT_BODY",BODY,{"disambiguationData":[OSD([sQuery(id+"F15.wireOp",EDGE,"E77.bottom"),sQuery(id+"F15.wireOp",EDGE,"E77.top"),sQuery(id+"F15.wireOp",EDGE,"E77.left"),sQuery(id+"F15.wireOp",EDGE,"E77.right")])]});
            transform(context, id + "F23", {"entities" : qUnion([Q0]), "transformType" : TransformType.TRANSLATION_3D, "dx" : 0 * mm, "dy" : 0 * mm, "dz" : -146.05 * mm, "makeCopy" : true});
        }
        {
            var Q0;
            Q0=makeQuery(id+"F22.opExtrude","SWEPT_BODY",BODY,{"disambiguationData":[OSD([sQuery(id+"F21.wireOp",EDGE,"E87.bottom"),sQuery(id+"F21.wireOp",EDGE,"E87.top"),sQuery(id+"F21.wireOp",EDGE,"E87.left"),sQuery(id+"F21.wireOp",EDGE,"E87.right")])]});
            transform(context, id + "F24", {"entities" : qUnion([Q0]), "transformType" : TransformType.TRANSLATION_3D, "dx" : 0 * mm, "dy" : 0 * mm, "dz" : -146.05 * mm, "makeCopy" : true});
        }
        {
            var Q0;
            Q0=makeQuery(id+"F1.opExtrude","SWEPT_FACE",FACE,{"disambiguationData":[OSD([sQuery(id+"F0.wireOp",EDGE,"E1.top")])]});
            var sketch = newSketch(context, id + "F25", { "sketchPlane" : qUnion([Q0])});
            skLineSegment(sketch, "E88", {"start": v(-527.3, 495.3) * mm, "end": v(-527.3, 0) * mm, "construction": true});
            skLineSegment(sketch, "E89", {"start": v(-684.21, 622.3) * mm, "end": v(-684.21, 0) * mm, "construction": true});
            skLineSegment(sketch, "E90", {"start": v(-217.49, 622.3) * mm, "end": v(-217.49, 0) * mm, "construction": true});
            skLineSegment(sketch, "E91.bottom", {"start": v(-665.16, 476.25) * mm, "end": v(-236.54, 476.25) * mm});
            skLineSegment(sketch, "E91.top", {"start": v(-665.16, 254) * mm, "end": v(-236.54, 254) * mm});
            skLineSegment(sketch, "E91.left", {"start": v(-665.16, 476.25) * mm, "end": v(-665.16, 254) * mm});
            skLineSegment(sketch, "E91.right", {"start": v(-236.54, 476.25) * mm, "end": v(-236.54, 254) * mm});
            skSolve(sketch);
        }
        {
            var Q0;
            Q0=makeQuery(id+"F25.imprint","IMPRINT",FACE,{"disambiguationData":[TD([[makeQuery(id+"F25.imprint","IMPRINT",EDGE,{"derivedFrom":sQuery(id+"F25.wireOp",EDGE,"eQZwb3qE-Jfpn-ImWK-ni1V-L1tkkNql1EaL.bottom")}),-1.0]])]});
            var Q1;
            Q1=makeQuery(id+"F25.imprint","IMPRINT",FACE,{"disambiguationData":[TD([[makeQuery(id+"F25.imprint","IMPRINT",EDGE,{"derivedFrom":sQuery(id+"F25.wireOp",EDGE,"E91.bottom")}),-1.0]])]});
            extrude(context, id + "F26", {"entities" : qUnion([Q0, Q1]), "oppositeDirection" : true, "depth" : 19.05 * mm});
        }
        {
            var Q0;
            Q0=makeQuery(id+"F26.opExtrude","SWEPT_FACE",FACE,{"disambiguationData":[OSD([sQuery(id+"F25.wireOp",EDGE,"E91.bottom")])]});
            var sketch = newSketch(context, id + "F27", { "sketchPlane" : qUnion([Q0])});
            skLineSegment(sketch, "E92.bottom", {"start": v(-236.54, -419.1) * mm, "end": v(-217.49, -419.1) * mm});
            skLineSegment(sketch, "E92.top", {"start": v(-236.54, -31.75) * mm, "end": v(-217.49, -31.75) * mm});
            skLineSegment(sketch, "E92.left", {"start": v(-236.54, -419.1) * mm, "end": v(-236.54, -31.75) * mm});
            skLineSegment(sketch, "E92.right", {"start": v(-217.49, -419.1) * mm, "end": v(-217.49, -31.75) * mm});
            skLineSegment(sketch, "E93", {"start": v(-450.85, -400.05) * mm, "end": v(-450.85, 87.74) * mm, "construction": true});
            skLineSegment(sketch, "E94.MirrorCS", {"start": v(-665.16, -419.1) * mm, "end": v(-684.21, -419.1) * mm});
            skLineSegment(sketch, "E95.MirrorCS", {"start": v(-665.16, -31.75) * mm, "end": v(-684.21, -31.75) * mm});
            skLineSegment(sketch, "E96.MirrorCS", {"start": v(-684.21, -419.1) * mm, "end": v(-684.21, -31.75) * mm});
            skLineSegment(sketch, "E97.MirrorCS", {"start": v(-665.16, -419.1) * mm, "end": v(-665.16, -31.75) * mm});
            skLineSegment(sketch, "E98.bottom", {"start": v(-684.21, -12.7) * mm, "end": v(-217.49, -12.7) * mm});
            skLineSegment(sketch, "E98.top", {"start": v(-684.21, -31.75) * mm, "end": v(-217.49, -31.75) * mm});
            skLineSegment(sketch, "E98.left", {"start": v(-684.21, -12.7) * mm, "end": v(-684.21, -31.75) * mm});
            skLineSegment(sketch, "E98.right", {"start": v(-217.49, -12.7) * mm, "end": v(-217.49, -31.75) * mm});
            skSolve(sketch);
        }
        {
            var Q0;
            {var subQ4=sQuery(id+"F27.wireOp",EDGE,"E94.MirrorCS");Q0=makeQuery(id+"F27.imprint","IMPRINT",FACE,{"disambiguationData":[TD([[makeQuery(id+"F27.imprint","IMPRINT",EDGE,{"derivedFrom":subQ4}),-1.0]])]});}
            var Q1;
            {var subQ1=sQuery(id+"F27.wireOp",EDGE,"E92.bottom");Q1=makeQuery(id+"F27.imprint","IMPRINT",FACE,{"disambiguationData":[TD([[makeQuery(id+"F27.imprint","IMPRINT",EDGE,{"derivedFrom":subQ1}),1.0]])]});}
            var Q2;
            Q2=makeQuery(id+"F27.imprint","IMPRINT",FACE,{"disambiguationData":[TD([[makeQuery(id+"F27.imprint","IMPRINT",EDGE,{"derivedFrom":sQuery(id+"F27.wireOp",EDGE,"E98.bottom")}),-1.0]])]});
            extrude(context, id + "F28", {"entities" : qUnion([Q0, Q1, Q2]), "operationType" : NewBodyOperationType.ADD, "oppositeDirection" : true, "depth" : 222.25 * mm});
        }
        {
            var Q0;
            Q0=makeQuery(id+"F28.boolean.opBoolean","MERGE",FACE,{"derivedFrom":[makeQuery(id+"F26.opExtrude","SWEPT_FACE",FACE,{"disambiguationData":[OSD([sQuery(id+"F25.wireOp",EDGE,"E91.top")])]}),makeQuery(id+"F28.opExtrude","CAP_FACE",FACE,{"disambiguationData":[OSD([sQuery(id+"F27.wireOp",EDGE,"E92.bottom"),sQuery(id+"F27.wireOp",EDGE,"E92.left"),sQuery(id+"F27.wireOp",EDGE,"E92.right"),sQuery(id+"F27.wireOp",EDGE,"E94.MirrorCS"),sQuery(id+"F27.wireOp",EDGE,"E96.MirrorCS"),sQuery(id+"F27.wireOp",EDGE,"E97.MirrorCS"),sQuery(id+"F27.wireOp",EDGE,"E98.bottom"),sQuery(id+"F27.wireOp",EDGE,"E98.top"),sQuery(id+"F27.wireOp",EDGE,"E98.left"),sQuery(id+"F27.wireOp",EDGE,"E98.right")])],"isStart":false})]});
            var sketch = newSketch(context, id + "F29", { "sketchPlane" : qUnion([Q0])});
            skLineSegment(sketch, "E99.bottom", {"start": v(-665.16, 400.05) * mm, "end": v(-236.54, 400.05) * mm});
            skLineSegment(sketch, "E99.top", {"start": v(-665.16, 31.75) * mm, "end": v(-236.54, 31.75) * mm});
            skLineSegment(sketch, "E99.left", {"start": v(-665.16, 400.05) * mm, "end": v(-665.16, 31.75) * mm});
            skLineSegment(sketch, "E99.right", {"start": v(-236.54, 400.05) * mm, "end": v(-236.54, 31.75) * mm});
            skSolve(sketch);
        }
        {
            var Q0;
            Q0=makeQuery(id+"F29.imprint","IMPRINT",FACE,{"disambiguationData":[TD([[makeQuery(id+"F29.imprint","IMPRINT",EDGE,{"derivedFrom":sQuery(id+"F29.wireOp",EDGE,"E99.bottom")}),-1.0]])]});
            extrude(context, id + "F30", {"entities" : qUnion([Q0]), "operationType" : NewBodyOperationType.ADD, "oppositeDirection" : true, "depth" : 19.05 * mm});
        }
        {
            var Q0;
            Q0=makeQuery(id+"F28.boolean.opBoolean","MERGE",FACE,{"derivedFrom":[makeQuery(id+"F26.opExtrude","CAP_FACE",FACE,{"disambiguationData":[OSD([sQuery(id+"F25.wireOp",EDGE,"E91.bottom"),sQuery(id+"F25.wireOp",EDGE,"E91.top"),sQuery(id+"F25.wireOp",EDGE,"E91.left"),sQuery(id+"F25.wireOp",EDGE,"E91.right")])],"isStart":true}),makeQuery(id+"F28.opExtrude","SWEPT_FACE",FACE,{"disambiguationData":[OSD([sQuery(id+"F27.wireOp",EDGE,"E92.bottom")])]}),makeQuery(id+"F28.opExtrude","SWEPT_FACE",FACE,{"disambiguationData":[OSD([sQuery(id+"F27.wireOp",EDGE,"E94.MirrorCS")])]})]});
            var sketch = newSketch(context, id + "F31", { "sketchPlane" : qUnion([Q0])});
            skLineSegment(sketch, "E100.bottom", {"start": v(-709.61, 488.95) * mm, "end": v(-192.09, 488.95) * mm});
            skLineSegment(sketch, "E100.top", {"start": v(-709.61, 254) * mm, "end": v(-192.09, 254) * mm});
            skLineSegment(sketch, "E100.left", {"start": v(-709.61, 488.95) * mm, "end": v(-709.61, 254) * mm});
            skLineSegment(sketch, "E100.right", {"start": v(-192.09, 488.95) * mm, "end": v(-192.09, 254) * mm});
            skSolve(sketch);
        }
        {
            var Q0;
            Q0 = qSketchRegion(id + "F31", true);
            extrude(context, id + "F32", {"entities" : qUnion([Q0]), "depth" : 19.05 * mm});
        }
        {
            var Q0;
            Q0=makeQuery(id+"F32.opExtrude","SWEPT_BODY",BODY,{"disambiguationData":[OSD([sQuery(id+"F31.wireOp",EDGE,"E100.bottom"),sQuery(id+"F31.wireOp",EDGE,"E100.top"),sQuery(id+"F31.wireOp",EDGE,"E100.left"),sQuery(id+"F31.wireOp",EDGE,"E100.right")])]});
            transform(context, id + "F33", {"entities" : qUnion([Q0]), "transformType" : TransformType.TRANSLATION_3D, "dx" : 0 * mm, "dy" : 0 * mm, "dz" : -241.3 * mm, "makeCopy" : true});
        }
        {
            var Q0;
            Q0=makeQuery(id+"F26.opExtrude","SWEPT_BODY",BODY,{"disambiguationData":[OSD([sQuery(id+"F25.wireOp",EDGE,"E91.bottom"),sQuery(id+"F25.wireOp",EDGE,"E91.top"),sQuery(id+"F25.wireOp",EDGE,"E91.left"),sQuery(id+"F25.wireOp",EDGE,"E91.right")])]});
            transform(context, id + "F34", {"entities" : qUnion([Q0]), "transformType" : TransformType.TRANSLATION_3D, "dx" : 0 * mm, "dy" : 0 * mm, "dz" : -241.3 * mm, "makeCopy" : true});
        }
        {
            var Q0;
            Q0=makeQuery(id+"F34.opPattern","COPY",BODY,{"derivedFrom":makeQuery(id+"F26.opExtrude","SWEPT_BODY",BODY,{"disambiguationData":[OSD([sQuery(id+"F25.wireOp",EDGE,"E91.bottom"),sQuery(id+"F25.wireOp",EDGE,"E91.top"),sQuery(id+"F25.wireOp",EDGE,"E91.left"),sQuery(id+"F25.wireOp",EDGE,"E91.right")])]}),"instanceName":"1"});
            transform(context, id + "F35", {"entities" : qUnion([Q0]), "transformType" : TransformType.TRANSLATION_3D, "dx" : 901.7 * mm, "dy" : 0 * mm, "dz" : 0 * mm, "makeCopy" : true});
        }
        {
            var Q0;
            Q0=makeQuery(id+"F33.opPattern","COPY",BODY,{"derivedFrom":makeQuery(id+"F32.opExtrude","SWEPT_BODY",BODY,{"disambiguationData":[OSD([sQuery(id+"F31.wireOp",EDGE,"E100.bottom"),sQuery(id+"F31.wireOp",EDGE,"E100.top"),sQuery(id+"F31.wireOp",EDGE,"E100.left"),sQuery(id+"F31.wireOp",EDGE,"E100.right")])]}),"instanceName":"1"});
            transform(context, id + "F36", {"entities" : qUnion([Q0]), "transformType" : TransformType.TRANSLATION_3D, "dx" : 901.7 * mm, "dy" : 0 * mm, "dz" : 0 * mm, "makeCopy" : true});
        }
        {
            var Q0;
            Q0=makeQuery(id+"F16.opExtrude","SWEPT_BODY",BODY,{"disambiguationData":[OSD([sQuery(id+"F15.wireOp",EDGE,"E77.bottom"),sQuery(id+"F15.wireOp",EDGE,"E77.top"),sQuery(id+"F15.wireOp",EDGE,"E77.left"),sQuery(id+"F15.wireOp",EDGE,"E77.right")])]});
            transform(context, id + "F37", {"entities" : qUnion([Q0]), "transformType" : TransformType.TRANSLATION_3D, "dx" : 901.7 * mm, "dy" : 0 * mm, "dz" : 0 * mm, "makeCopy" : true});
        }
        {
            var Q0;
            Q0=makeQuery(id+"F22.opExtrude","SWEPT_BODY",BODY,{"disambiguationData":[OSD([sQuery(id+"F21.wireOp",EDGE,"E87.bottom"),sQuery(id+"F21.wireOp",EDGE,"E87.top"),sQuery(id+"F21.wireOp",EDGE,"E87.left"),sQuery(id+"F21.wireOp",EDGE,"E87.right")])]});
            transform(context, id + "F38", {"entities" : qUnion([Q0]), "transformType" : TransformType.TRANSLATION_3D, "dx" : 901.7 * mm, "dy" : 0 * mm, "dz" : 0 * mm, "makeCopy" : true});
        }
        {
            var Q0;
            Q0=makeQuery(id+"F24.opPattern","COPY",BODY,{"derivedFrom":makeQuery(id+"F22.opExtrude","SWEPT_BODY",BODY,{"disambiguationData":[OSD([sQuery(id+"F21.wireOp",EDGE,"E87.bottom"),sQuery(id+"F21.wireOp",EDGE,"E87.top"),sQuery(id+"F21.wireOp",EDGE,"E87.left"),sQuery(id+"F21.wireOp",EDGE,"E87.right")])]}),"instanceName":"1"});
            transform(context, id + "F39", {"entities" : qUnion([Q0]), "transformType" : TransformType.TRANSLATION_3D, "dx" : 901.7 * mm, "dy" : 0 * mm, "dz" : 0 * mm, "makeCopy" : true});
        }
        {
            var Q0;
            Q0=makeQuery(id+"F23.opPattern","COPY",BODY,{"derivedFrom":makeQuery(id+"F16.opExtrude","SWEPT_BODY",BODY,{"disambiguationData":[OSD([sQuery(id+"F15.wireOp",EDGE,"E77.bottom"),sQuery(id+"F15.wireOp",EDGE,"E77.top"),sQuery(id+"F15.wireOp",EDGE,"E77.left"),sQuery(id+"F15.wireOp",EDGE,"E77.right")])]}),"instanceName":"1"});
            transform(context, id + "F40", {"entities" : qUnion([Q0]), "transformType" : TransformType.TRANSLATION_3D, "dx" : 901.7 * mm, "dy" : 0 * mm, "dz" : 0 * mm, "makeCopy" : true});
        }
        {
            var Q0;
            Q0=makeQuery(id+"F26.opExtrude","SWEPT_BODY",BODY,{"disambiguationData":[OSD([sQuery(id+"F25.wireOp",EDGE,"E91.bottom"),sQuery(id+"F25.wireOp",EDGE,"E91.top"),sQuery(id+"F25.wireOp",EDGE,"E91.left"),sQuery(id+"F25.wireOp",EDGE,"E91.right")])]});
            transform(context, id + "F41", {"entities" : qUnion([Q0]), "transformType" : TransformType.TRANSLATION_3D, "dx" : 901.7 * mm, "dy" : 0 * mm, "dz" : 0 * mm, "makeCopy" : true});
        }
        {
            var Q0;
            Q0=makeQuery(id+"F32.opExtrude","SWEPT_BODY",BODY,{"disambiguationData":[OSD([sQuery(id+"F31.wireOp",EDGE,"E100.bottom"),sQuery(id+"F31.wireOp",EDGE,"E100.top"),sQuery(id+"F31.wireOp",EDGE,"E100.left"),sQuery(id+"F31.wireOp",EDGE,"E100.right")])]});
            transform(context, id + "F42", {"entities" : qUnion([Q0]), "transformType" : TransformType.TRANSLATION_3D, "dx" : 901.7 * mm, "dy" : 0 * mm, "dz" : 0 * mm, "makeCopy" : true});
        }
        {
            var Q0;
            Q0=makeQuery(id+"F16.opExtrude","SWEPT_BODY",BODY,{"disambiguationData":[OSD([sQuery(id+"F15.wireOp",EDGE,"E77.bottom"),sQuery(id+"F15.wireOp",EDGE,"E77.top"),sQuery(id+"F15.wireOp",EDGE,"E77.left"),sQuery(id+"F15.wireOp",EDGE,"E77.right")])]});
            var Q1;
            Q1=makeQuery(id+"F18.opExtrude","SWEPT_EDGE",EDGE,{"disambiguationData":[OSD([sQuery(id+"F17.wireOp",EDGE,"E85.top"),sQuery(id+"F17.wireOp",EDGE,"E85.right")])]});
            transform(context, id + "F43", {"entities" : qUnion([Q0]), "transformType" : TransformType.TRANSLATION_3D, "dx" : 0 * mm, "dy" : 412.75 * mm, "dz" : 0 * mm, "makeCopy" : true});
        }
        {
            var Q0;
            Q0=makeQuery(id+"F43.opPattern","COPY",BODY,{"derivedFrom":makeQuery(id+"F16.opExtrude","SWEPT_BODY",BODY,{"disambiguationData":[OSD([sQuery(id+"F15.wireOp",EDGE,"E77.bottom"),sQuery(id+"F15.wireOp",EDGE,"E77.top"),sQuery(id+"F15.wireOp",EDGE,"E77.left"),sQuery(id+"F15.wireOp",EDGE,"E77.right")])]}),"instanceName":"1"});
            deleteBodies(context, id + "F44", {"entities" : qUnion([Q0])});
        }
        {
            var Q0;
            Q0=makeQuery(id+"F16.opExtrude","SWEPT_BODY",BODY,{"disambiguationData":[OSD([sQuery(id+"F15.wireOp",EDGE,"E77.bottom"),sQuery(id+"F15.wireOp",EDGE,"E77.top"),sQuery(id+"F15.wireOp",EDGE,"E77.left"),sQuery(id+"F15.wireOp",EDGE,"E77.right")])]});
            transform(context, id + "F45", {"entities" : qUnion([Q0]), "transformType" : TransformType.TRANSLATION_3D, "dx" : 0 * mm, "dy" : 431.8 * mm, "dz" : 0 * mm, "makeCopy" : true});
        }
        {
            var Q0;
            Q0=makeQuery(id+"F22.opExtrude","SWEPT_BODY",BODY,{"disambiguationData":[OSD([sQuery(id+"F21.wireOp",EDGE,"E87.bottom"),sQuery(id+"F21.wireOp",EDGE,"E87.top"),sQuery(id+"F21.wireOp",EDGE,"E87.left"),sQuery(id+"F21.wireOp",EDGE,"E87.right")])]});
            transform(context, id + "F46", {"entities" : qUnion([Q0]), "transformType" : TransformType.TRANSLATION_3D, "dx" : 0 * mm, "dy" : 857.25 * mm, "dz" : 0 * mm, "makeCopy" : true});
        }
        {
            var Q0;
            Q0=makeQuery(id+"F23.opPattern","COPY",BODY,{"derivedFrom":makeQuery(id+"F16.opExtrude","SWEPT_BODY",BODY,{"disambiguationData":[OSD([sQuery(id+"F15.wireOp",EDGE,"E77.bottom"),sQuery(id+"F15.wireOp",EDGE,"E77.top"),sQuery(id+"F15.wireOp",EDGE,"E77.left"),sQuery(id+"F15.wireOp",EDGE,"E77.right")])]}),"instanceName":"1"});
            transform(context, id + "F47", {"entities" : qUnion([Q0]), "transformType" : TransformType.TRANSLATION_3D, "dx" : 0 * mm, "dy" : 431.8 * mm, "dz" : 0 * mm, "makeCopy" : true});
        }
        {
            var Q0;
            Q0=makeQuery(id+"F24.opPattern","COPY",BODY,{"derivedFrom":makeQuery(id+"F22.opExtrude","SWEPT_BODY",BODY,{"disambiguationData":[OSD([sQuery(id+"F21.wireOp",EDGE,"E87.bottom"),sQuery(id+"F21.wireOp",EDGE,"E87.top"),sQuery(id+"F21.wireOp",EDGE,"E87.left"),sQuery(id+"F21.wireOp",EDGE,"E87.right")])]}),"instanceName":"1"});
            transform(context, id + "F48", {"entities" : qUnion([Q0]), "transformType" : TransformType.TRANSLATION_3D, "dx" : 0 * mm, "dy" : 857.25 * mm, "dz" : 0 * mm, "makeCopy" : true});
        }
        {
            var Q0;
            Q0=makeQuery(id+"F26.opExtrude","SWEPT_BODY",BODY,{"disambiguationData":[OSD([sQuery(id+"F25.wireOp",EDGE,"E91.bottom"),sQuery(id+"F25.wireOp",EDGE,"E91.top"),sQuery(id+"F25.wireOp",EDGE,"E91.left"),sQuery(id+"F25.wireOp",EDGE,"E91.right")])]});
            transform(context, id + "F49", {"entities" : qUnion([Q0]), "transformType" : TransformType.TRANSLATION_3D, "dx" : 0 * mm, "dy" : 431.8 * mm, "dz" : 0 * mm, "makeCopy" : true});
        }
        {
            var Q0;
            Q0=makeQuery(id+"F32.opExtrude","SWEPT_BODY",BODY,{"disambiguationData":[OSD([sQuery(id+"F31.wireOp",EDGE,"E100.bottom"),sQuery(id+"F31.wireOp",EDGE,"E100.top"),sQuery(id+"F31.wireOp",EDGE,"E100.left"),sQuery(id+"F31.wireOp",EDGE,"E100.right")])]});
            transform(context, id + "F50", {"entities" : qUnion([Q0]), "transformType" : TransformType.TRANSLATION_3D, "dx" : 0 * mm, "dy" : 857.25 * mm, "dz" : 0 * mm, "makeCopy" : true});
        }
        {
            var Q0;
            Q0=makeQuery(id+"F34.opPattern","COPY",BODY,{"derivedFrom":makeQuery(id+"F26.opExtrude","SWEPT_BODY",BODY,{"disambiguationData":[OSD([sQuery(id+"F25.wireOp",EDGE,"E91.bottom"),sQuery(id+"F25.wireOp",EDGE,"E91.top"),sQuery(id+"F25.wireOp",EDGE,"E91.left"),sQuery(id+"F25.wireOp",EDGE,"E91.right")])]}),"instanceName":"1"});
            transform(context, id + "F51", {"entities" : qUnion([Q0]), "transformType" : TransformType.TRANSLATION_3D, "dx" : 0 * mm, "dy" : 431.8 * mm, "dz" : 0 * mm, "makeCopy" : true});
        }
        {
            var Q0;
            Q0=makeQuery(id+"F33.opPattern","COPY",BODY,{"derivedFrom":makeQuery(id+"F32.opExtrude","SWEPT_BODY",BODY,{"disambiguationData":[OSD([sQuery(id+"F31.wireOp",EDGE,"E100.bottom"),sQuery(id+"F31.wireOp",EDGE,"E100.top"),sQuery(id+"F31.wireOp",EDGE,"E100.left"),sQuery(id+"F31.wireOp",EDGE,"E100.right")])]}),"instanceName":"1"});
            transform(context, id + "F52", {"entities" : qUnion([Q0]), "transformType" : TransformType.TRANSLATION_3D, "dx" : 0 * mm, "dy" : 857.25 * mm, "dz" : 0 * mm, "makeCopy" : true});
        }
        {
            var Q0;
            Q0=makeQuery(id+"F37.opPattern","COPY",BODY,{"derivedFrom":makeQuery(id+"F16.opExtrude","SWEPT_BODY",BODY,{"disambiguationData":[OSD([sQuery(id+"F15.wireOp",EDGE,"E77.bottom"),sQuery(id+"F15.wireOp",EDGE,"E77.top"),sQuery(id+"F15.wireOp",EDGE,"E77.left"),sQuery(id+"F15.wireOp",EDGE,"E77.right")])]}),"instanceName":"1"});
            transform(context, id + "F53", {"entities" : qUnion([Q0]), "transformType" : TransformType.TRANSLATION_3D, "dx" : 0 * mm, "dy" : 431.8 * mm, "dz" : 0 * mm, "makeCopy" : true});
        }
        {
            var Q0;
            Q0=makeQuery(id+"F38.opPattern","COPY",BODY,{"derivedFrom":makeQuery(id+"F22.opExtrude","SWEPT_BODY",BODY,{"disambiguationData":[OSD([sQuery(id+"F21.wireOp",EDGE,"E87.bottom"),sQuery(id+"F21.wireOp",EDGE,"E87.top"),sQuery(id+"F21.wireOp",EDGE,"E87.left"),sQuery(id+"F21.wireOp",EDGE,"E87.right")])]}),"instanceName":"1"});
            transform(context, id + "F54", {"entities" : qUnion([Q0]), "transformType" : TransformType.TRANSLATION_3D, "dx" : 0 * mm, "dy" : 857.25 * mm, "dz" : 0 * mm, "makeCopy" : true});
        }
        {
            var Q0;
            Q0=makeQuery(id+"F40.opPattern","COPY",BODY,{"derivedFrom":makeQuery(id+"F23.opPattern","COPY",BODY,{"derivedFrom":makeQuery(id+"F16.opExtrude","SWEPT_BODY",BODY,{"disambiguationData":[OSD([sQuery(id+"F15.wireOp",EDGE,"E77.bottom"),sQuery(id+"F15.wireOp",EDGE,"E77.top"),sQuery(id+"F15.wireOp",EDGE,"E77.left"),sQuery(id+"F15.wireOp",EDGE,"E77.right")])]}),"instanceName":"1"}),"instanceName":"1"});
            transform(context, id + "F55", {"entities" : qUnion([Q0]), "transformType" : TransformType.TRANSLATION_3D, "dx" : 0 * mm, "dy" : 431.8 * mm, "dz" : 0 * mm, "makeCopy" : true});
        }
        {
            var Q0;
            Q0=makeQuery(id+"F39.opPattern","COPY",BODY,{"derivedFrom":makeQuery(id+"F24.opPattern","COPY",BODY,{"derivedFrom":makeQuery(id+"F22.opExtrude","SWEPT_BODY",BODY,{"disambiguationData":[OSD([sQuery(id+"F21.wireOp",EDGE,"E87.bottom"),sQuery(id+"F21.wireOp",EDGE,"E87.top"),sQuery(id+"F21.wireOp",EDGE,"E87.left"),sQuery(id+"F21.wireOp",EDGE,"E87.right")])]}),"instanceName":"1"}),"instanceName":"1"});
            transform(context, id + "F56", {"entities" : qUnion([Q0]), "transformType" : TransformType.TRANSLATION_3D, "dx" : 0 * mm, "dy" : 857.25 * mm, "dz" : 0 * mm, "makeCopy" : true});
        }
        {
            var Q0;
            Q0=makeQuery(id+"F41.opPattern","COPY",BODY,{"derivedFrom":makeQuery(id+"F26.opExtrude","SWEPT_BODY",BODY,{"disambiguationData":[OSD([sQuery(id+"F25.wireOp",EDGE,"E91.bottom"),sQuery(id+"F25.wireOp",EDGE,"E91.top"),sQuery(id+"F25.wireOp",EDGE,"E91.left"),sQuery(id+"F25.wireOp",EDGE,"E91.right")])]}),"instanceName":"1"});
            transform(context, id + "F57", {"entities" : qUnion([Q0]), "transformType" : TransformType.TRANSLATION_3D, "dx" : 0 * mm, "dy" : 431.8 * mm, "dz" : 0 * mm, "makeCopy" : true});
        }
        {
            var Q0;
            Q0=makeQuery(id+"F42.opPattern","COPY",BODY,{"derivedFrom":makeQuery(id+"F32.opExtrude","SWEPT_BODY",BODY,{"disambiguationData":[OSD([sQuery(id+"F31.wireOp",EDGE,"E100.bottom"),sQuery(id+"F31.wireOp",EDGE,"E100.top"),sQuery(id+"F31.wireOp",EDGE,"E100.left"),sQuery(id+"F31.wireOp",EDGE,"E100.right")])]}),"instanceName":"1"});
            transform(context, id + "F58", {"entities" : qUnion([Q0]), "transformType" : TransformType.TRANSLATION_3D, "dx" : 0 * mm, "dy" : 857.25 * mm, "dz" : 0 * mm, "makeCopy" : true});
        }
        {
            var Q0;
            Q0=makeQuery(id+"F35.opPattern","COPY",BODY,{"derivedFrom":makeQuery(id+"F34.opPattern","COPY",BODY,{"derivedFrom":makeQuery(id+"F26.opExtrude","SWEPT_BODY",BODY,{"disambiguationData":[OSD([sQuery(id+"F25.wireOp",EDGE,"E91.bottom"),sQuery(id+"F25.wireOp",EDGE,"E91.top"),sQuery(id+"F25.wireOp",EDGE,"E91.left"),sQuery(id+"F25.wireOp",EDGE,"E91.right")])]}),"instanceName":"1"}),"instanceName":"1"});
            transform(context, id + "F59", {"entities" : qUnion([Q0]), "transformType" : TransformType.TRANSLATION_3D, "dx" : 0 * mm, "dy" : 431.8 * mm, "dz" : 0 * mm, "makeCopy" : true});
        }
        {
            var Q0;
            Q0=makeQuery(id+"F36.opPattern","COPY",BODY,{"derivedFrom":makeQuery(id+"F33.opPattern","COPY",BODY,{"derivedFrom":makeQuery(id+"F32.opExtrude","SWEPT_BODY",BODY,{"disambiguationData":[OSD([sQuery(id+"F31.wireOp",EDGE,"E100.bottom"),sQuery(id+"F31.wireOp",EDGE,"E100.top"),sQuery(id+"F31.wireOp",EDGE,"E100.left"),sQuery(id+"F31.wireOp",EDGE,"E100.right")])]}),"instanceName":"1"}),"instanceName":"1"});
            transform(context, id + "F60", {"entities" : qUnion([Q0]), "transformType" : TransformType.TRANSLATION_3D, "dx" : 0 * mm, "dy" : 857.25 * mm, "dz" : 0 * mm, "makeCopy" : true});
        }
        {
            var Q0;
            Q0=makeQuery(id+"F3.opExtrude","CAP_FACE",FACE,{"disambiguationData":[OSD([sQuery(id+"F2.wireOp",EDGE,"E24.bottom"),sQuery(id+"F2.wireOp",EDGE,"E24.top"),sQuery(id+"F2.wireOp",EDGE,"E24.left"),sQuery(id+"F2.wireOp",EDGE,"E24.right")])],"isStart":false});
            var sketch = newSketch(context, id + "F61", { "sketchPlane" : qUnion([Q0])});
            skLineSegment(sketch, "E101.bottom", {"start": v(-736.6, 381) * mm, "end": v(-660.4, 381) * mm});
            skLineSegment(sketch, "E101.top", {"start": v(-736.6, 368.3) * mm, "end": v(-660.4, 368.3) * mm});
            skLineSegment(sketch, "E101.left", {"start": v(-736.6, 381) * mm, "end": v(-736.6, 368.3) * mm});
            skLineSegment(sketch, "E101.right", {"start": v(-660.4, 381) * mm, "end": v(-660.4, 368.3) * mm});
            skLineSegment(sketch, "E102.MirrorCS", {"start": v(660.4, 381) * mm, "end": v(660.4, 368.3) * mm});
            skLineSegment(sketch, "E103.MirrorCS", {"start": v(736.6, 381) * mm, "end": v(736.6, 368.3) * mm});
            skLineSegment(sketch, "E104.MirrorCS", {"start": v(736.6, 368.3) * mm, "end": v(660.4, 368.3) * mm});
            skLineSegment(sketch, "E105.MirrorCS", {"start": v(736.6, 381) * mm, "end": v(660.4, 381) * mm});
            skLineSegment(sketch, "E106.MirrorCS", {"start": v(736.6, -381) * mm, "end": v(736.6, -368.3) * mm});
            skLineSegment(sketch, "E107.MirrorCS", {"start": v(-660.4, -381) * mm, "end": v(-660.4, -368.3) * mm});
            skLineSegment(sketch, "E108.MirrorCS", {"start": v(660.4, -381) * mm, "end": v(660.4, -368.3) * mm});
            skLineSegment(sketch, "E109.MirrorCS", {"start": v(-736.6, -381) * mm, "end": v(-736.6, -368.3) * mm});
            skLineSegment(sketch, "E110.MirrorCS", {"start": v(736.6, -368.3) * mm, "end": v(660.4, -368.3) * mm});
            skLineSegment(sketch, "E111.MirrorCS", {"start": v(-736.6, -368.3) * mm, "end": v(-660.4, -368.3) * mm});
            skLineSegment(sketch, "E112.MirrorCS", {"start": v(736.6, -381) * mm, "end": v(660.4, -381) * mm});
            skLineSegment(sketch, "E113.MirrorCS", {"start": v(-736.6, -381) * mm, "end": v(-660.4, -381) * mm});
            skSolve(sketch);
        }
        {
            var Q0;
            Q0 = qSketchRegion(id + "F61", true);
            extrude(context, id + "F62", {"entities" : qUnion([Q0]), "oppositeDirection" : true, "depth" : 88.9 * mm});
        }
        {
            var Q0;
            Q0=makeQuery(id+"F3.opExtrude","CAP_FACE",FACE,{"disambiguationData":[OSD([sQuery(id+"F2.wireOp",EDGE,"E24.bottom"),sQuery(id+"F2.wireOp",EDGE,"E24.top"),sQuery(id+"F2.wireOp",EDGE,"E24.left"),sQuery(id+"F2.wireOp",EDGE,"E24.right")])],"isStart":false});
            var sketch = newSketch(context, id + "F63", { "sketchPlane" : qUnion([Q0])});
            skCircle(sketch, "E114", {"center": v(-723.9, 387.35) * mm, "radius": 6.35 * mm});
            skCircle(sketch, "E115.MirrorC", {"center": v(723.9, 387.35) * mm, "radius": 6.35 * mm});
            skCircle(sketch, "E116.MirrorC", {"center": v(-723.9, -387.35) * mm, "radius": 6.35 * mm});
            skCircle(sketch, "E117.MirrorC", {"center": v(723.9, -387.35) * mm, "radius": 6.35 * mm});
            skSolve(sketch);
        }
        {
            var Q0;
            Q0 = qSketchRegion(id + "F63", true);
            extrude(context, id + "F64", {"entities" : qUnion([Q0]), "depth" : 25.4 * mm});
        }
        {
            var Q0;
            Q0=makeQuery(id+"F64.opExtrude","CAP_FACE",FACE,{"disambiguationData":[OSD([sQuery(id+"F63.wireOp",EDGE,"E114")])],"isStart":false});
            var sketch = newSketch(context, id + "F65", { "sketchPlane" : qUnion([Q0])});
            skCircle(sketch, "E118", {"center": v(-723.9, 387.35) * mm, "radius": 19.05 * mm});
            skCircle(sketch, "E119.MirrorC", {"center": v(723.9, 387.35) * mm, "radius": 19.05 * mm});
            skCircle(sketch, "E120.MirrorC", {"center": v(-723.9, -387.35) * mm, "radius": 19.05 * mm});
            skCircle(sketch, "E121.MirrorC", {"center": v(723.9, -387.35) * mm, "radius": 19.05 * mm});
            skSolve(sketch);
        }
        {
            var Q0;
            Q0 = qSketchRegion(id + "F65", true);
            extrude(context, id + "F66", {"entities" : qUnion([Q0]), "depth" : 12.7 * mm});
        }
    });
